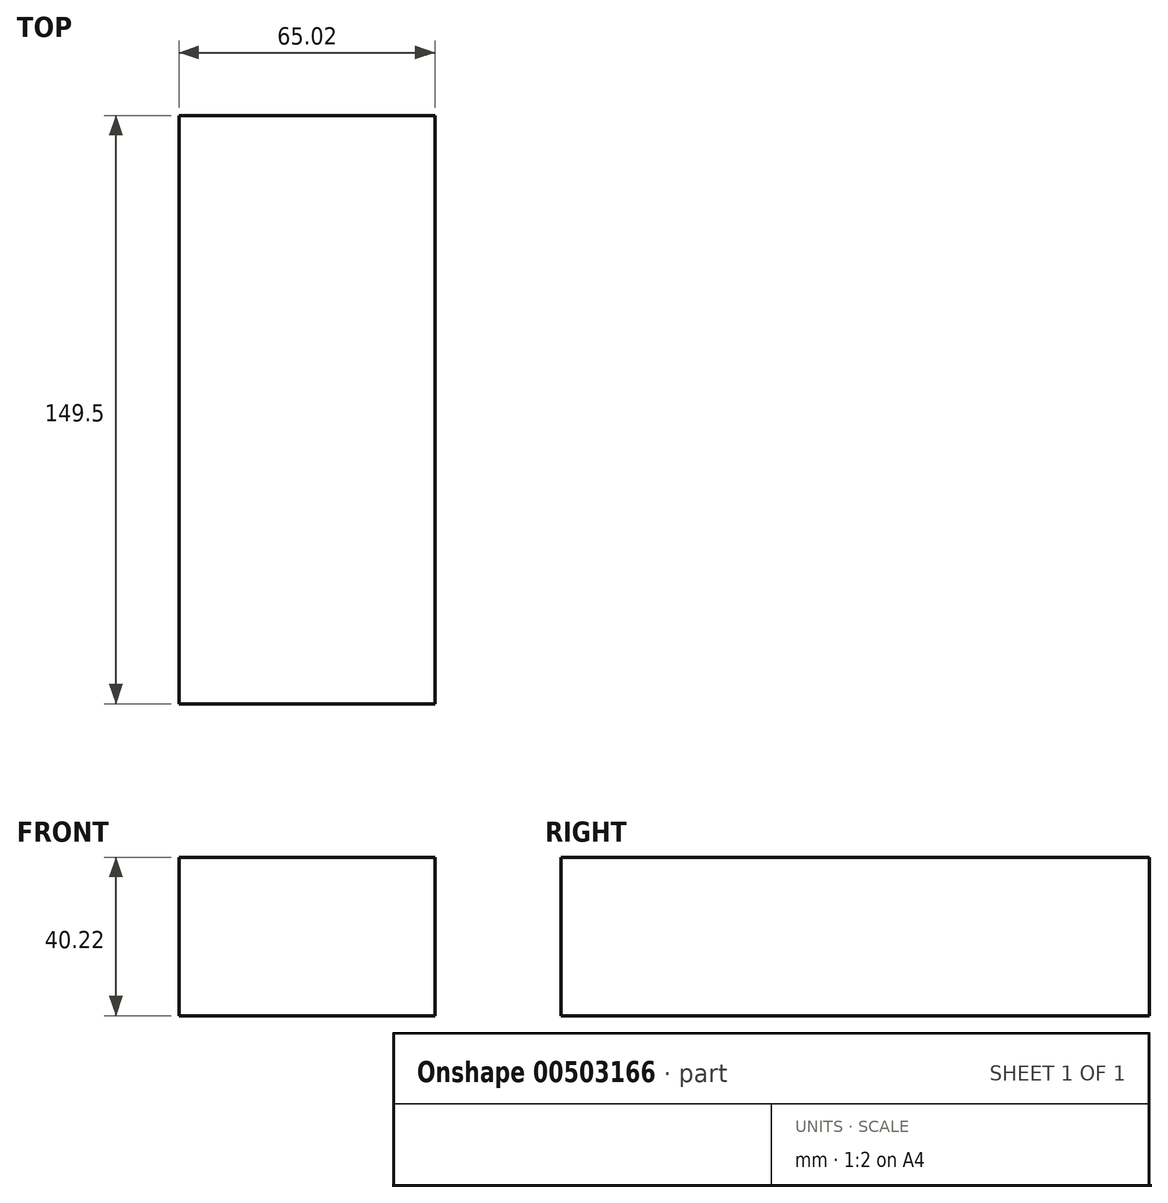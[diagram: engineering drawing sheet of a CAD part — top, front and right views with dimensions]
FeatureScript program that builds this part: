
annotation { "Feature Type Name" : "Feature", "Feature Type Description" : "" }
export const myFeature = defineFeature(function(context is Context, id is Id, definition is map)
    precondition{}
    {
        {
            var Q0;
            Q0=qCreatedBy(makeId("Top.planeOp"),FACE);
            var sketch = newSketch(context, id + "F0", { "sketchPlane" : qUnion([Q0])});
            skLineSegment(sketch, "E0.bottom", {"start": v(-65.02, 0) * mm, "end": v(0, 0) * mm});
            skLineSegment(sketch, "E0.top", {"start": v(-65.02, 149.5) * mm, "end": v(0, 149.5) * mm});
            skLineSegment(sketch, "E0.left", {"start": v(-65.02, 0) * mm, "end": v(-65.02, 149.5) * mm});
            skLineSegment(sketch, "E0.right", {"start": v(0, 0) * mm, "end": v(0, 149.5) * mm});
            skSolve(sketch);
        }
        {
            var Q0;
            Q0 = qSketchRegion(id + "F0", true);
            extrude(context, id + "F1", {"entities" : qUnion([Q0]), "depth" : 40.22 * mm});
        }
    });
